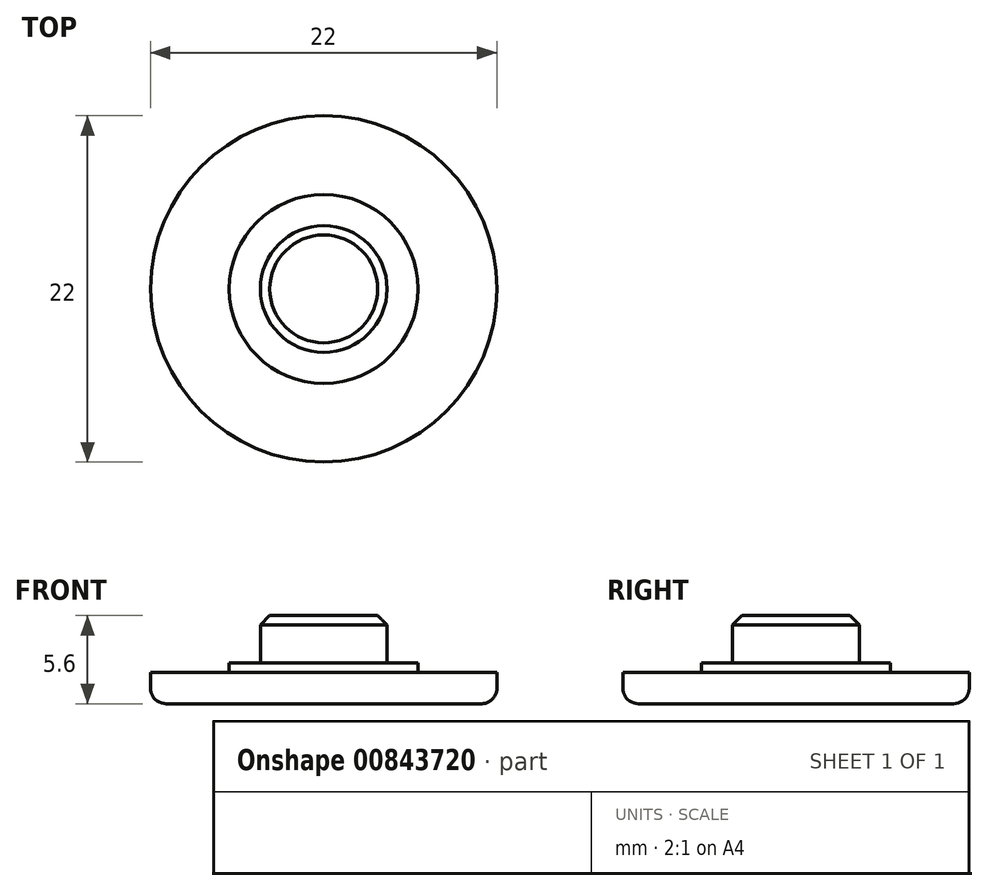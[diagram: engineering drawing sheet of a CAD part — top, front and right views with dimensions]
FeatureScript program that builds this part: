
annotation { "Feature Type Name" : "Feature", "Feature Type Description" : "" }
export const myFeature = defineFeature(function(context is Context, id is Id, definition is map)
    precondition{}
    {
        {
            var Q0;
            Q0=qCreatedBy(makeId("Top.planeOp"),FACE);
            var sketch = newSketch(context, id + "F0", { "sketchPlane" : qUnion([Q0])});
            skCircle(sketch, "E0", {"center": v(0, 0) * mm, "radius": 11 * mm});
            skCircle(sketch, "E1", {"center": v(0, 0) * mm, "radius": 6 * mm});
            skCircle(sketch, "E2", {"center": v(0, 0) * mm, "radius": 4.03 * mm});
            skSolve(sketch);
        }
        {
            var Q0;
            Q0=makeQuery(id+"F0.imprint","IMPRINT",FACE,{"disambiguationData":[TD([[makeQuery(id+"F0.imprint","IMPRINT",EDGE,{"derivedFrom":sQuery(id+"F0.wireOp",EDGE,"E0")}),1.0]])]});
            var Q1;
            Q1=makeQuery(id+"F0.imprint","IMPRINT",FACE,{"disambiguationData":[TD([[makeQuery(id+"F0.imprint","IMPRINT",EDGE,{"derivedFrom":sQuery(id+"F0.wireOp",EDGE,"E1")}),1.0]])]});
            var Q2;
            Q2=makeQuery(id+"F0.imprint","IMPRINT",FACE,{"disambiguationData":[TD([[makeQuery(id+"F0.imprint","IMPRINT",EDGE,{"derivedFrom":sQuery(id+"F0.wireOp",EDGE,"E2")}),1.0]])]});
            extrude(context, id + "F1", {"entities" : qUnion([Q0, Q1, Q2]), "oppositeDirection" : true, "depth" : 2 * mm, "offsetDistance" : 25 * mm});
        }
        {
            var Q0;
            Q0=makeQuery(id+"F0.imprint","IMPRINT",FACE,{"disambiguationData":[TD([[makeQuery(id+"F0.imprint","IMPRINT",EDGE,{"derivedFrom":sQuery(id+"F0.wireOp",EDGE,"E1")}),1.0]])]});
            extrude(context, id + "F2", {"entities" : qUnion([Q0]), "operationType" : NewBodyOperationType.ADD, "depth" : 0.6 * mm, "offsetDistance" : 25 * mm});
        }
        {
            var Q0;
            Q0=makeQuery(id+"F0.imprint","IMPRINT",FACE,{"disambiguationData":[TD([[makeQuery(id+"F0.imprint","IMPRINT",EDGE,{"derivedFrom":sQuery(id+"F0.wireOp",EDGE,"E2")}),1.0]])]});
            extrude(context, id + "F3", {"entities" : qUnion([Q0]), "operationType" : NewBodyOperationType.ADD, "depth" : (3 + 0.6) * mm, "offsetDistance" : 25 * mm});
        }
        {
            var Q0;
            Q0=makeQuery(id+"F1.opExtrude","CAP_EDGE",EDGE,{"disambiguationData":[OSD([sQuery(id+"F0.wireOp",EDGE,"E0")])],"isStart":false});
            fillet(context, id + "F4", {"entities" : qUnion([Q0]), "radius" : 1 * mm, "tangentPropagation" : true, "allowEdgeOverflow" : false});
        }
        {
            var Q0;
            Q0=makeQuery(id+"F3.opExtrude","CAP_EDGE",EDGE,{"disambiguationData":[OSD([sQuery(id+"F0.wireOp",EDGE,"E2")])],"isStart":false});
            chamfer(context, id + "F5", {"entities" : qUnion([Q0]), "width" : 0.6 * mm, "tangentPropagation" : true});
        }
    });
